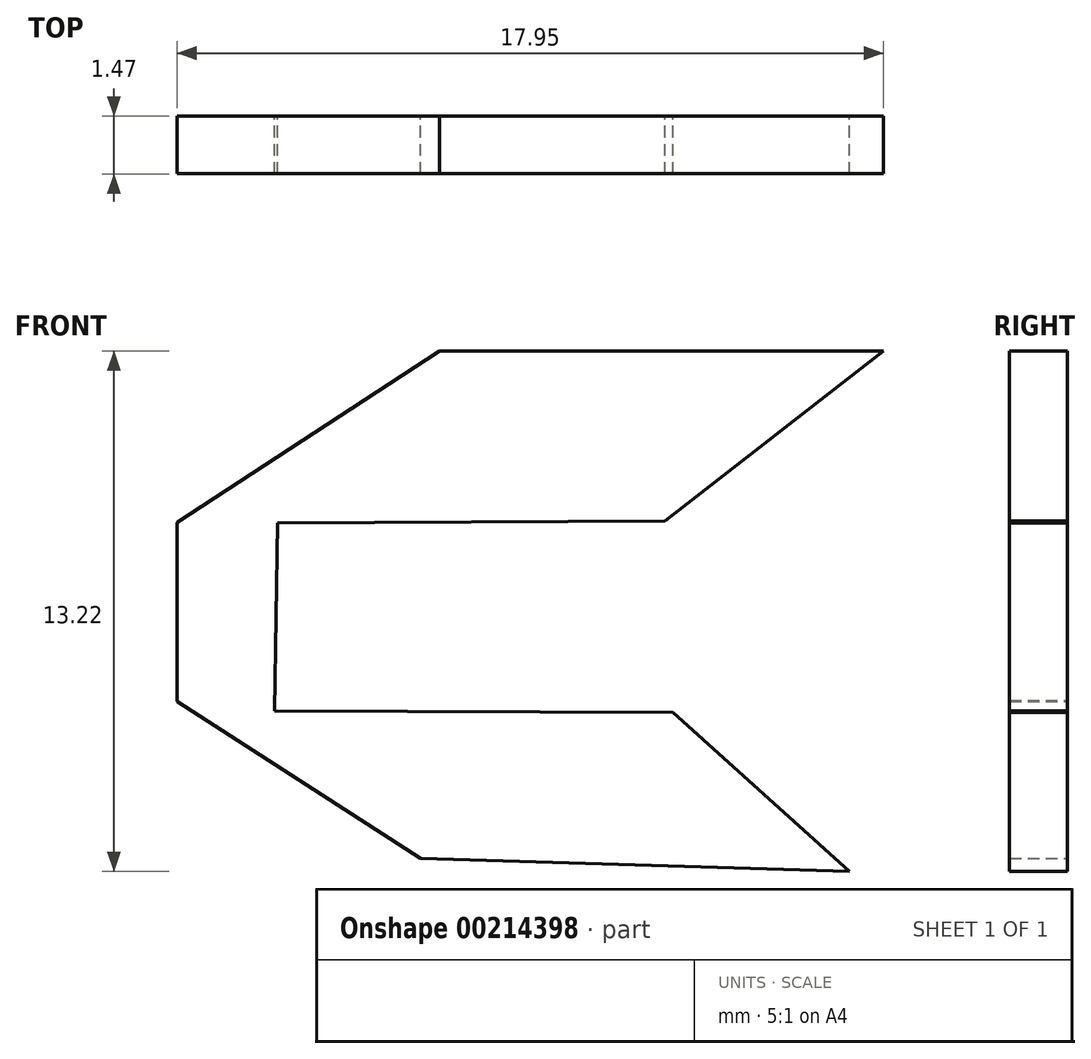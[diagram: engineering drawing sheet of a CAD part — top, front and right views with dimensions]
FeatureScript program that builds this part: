
annotation { "Feature Type Name" : "Feature", "Feature Type Description" : "" }
export const myFeature = defineFeature(function(context is Context, id is Id, definition is map)
    precondition{}
    {
        {
            var Q0;
            Q0=qCreatedBy(makeId("Front.planeOp"),FACE);
            var sketch = newSketch(context, id + "F0", { "sketchPlane" : qUnion([Q0])});
            skLineSegment(sketch, "E0", {"start": v(-22.64, 0) * mm, "end": v(-22.64, 2.44) * mm});
            skLineSegment(sketch, "E1", {"start": v(-22.64, 2.44) * mm, "end": v(-22.64, 0) * mm});
            skLineSegment(sketch, "E2", {"start": v(-22.64, 0) * mm, "end": v(-22.64, -2.08) * mm});
            skLineSegment(sketch, "E3", {"start": v(-22.64, 2.44) * mm, "end": v(-15.97, 6.8) * mm});
            skLineSegment(sketch, "E4", {"start": v(-15.97, 6.8) * mm, "end": v(-4.7, 6.8) * mm});
            skLineSegment(sketch, "E5", {"start": v(-4.7, 6.8) * mm, "end": v(-10.25, 2.48) * mm});
            skLineSegment(sketch, "E6", {"start": v(-10.25, 2.48) * mm, "end": v(-20.1, 2.43) * mm});
            skLineSegment(sketch, "E7", {"start": v(-20.1, 2.43) * mm, "end": v(-20.18, -2.34) * mm});
            skLineSegment(sketch, "E8", {"start": v(-20.18, -2.34) * mm, "end": v(-10.05, -2.38) * mm});
            skLineSegment(sketch, "E9", {"start": v(-10.05, -2.38) * mm, "end": v(-10.05, -2.38) * mm});
            skLineSegment(sketch, "E10", {"start": v(-10.05, -2.38) * mm, "end": v(-5.57, -6.42) * mm});
            skLineSegment(sketch, "E11", {"start": v(-5.57, -6.42) * mm, "end": v(-16.46, -6.1) * mm});
            skLineSegment(sketch, "E12", {"start": v(-16.46, -6.1) * mm, "end": v(-22.65, -2.1) * mm});
            skLineSegment(sketch, "E13", {"start": v(-22.65, -2.1) * mm, "end": v(-22.65, -2.1) * mm});
            skLineSegment(sketch, "E14", {"start": v(-22.65, -2.1) * mm, "end": v(-22.64, -2.08) * mm});
            skSolve(sketch);
        }
        {
            var Q0;
            Q0 = qSketchRegion(id + "F0", true);
            extrude(context, id + "F1", {"entities" : qUnion([Q0]), "depth" : 1.47 * mm});
        }
    });
